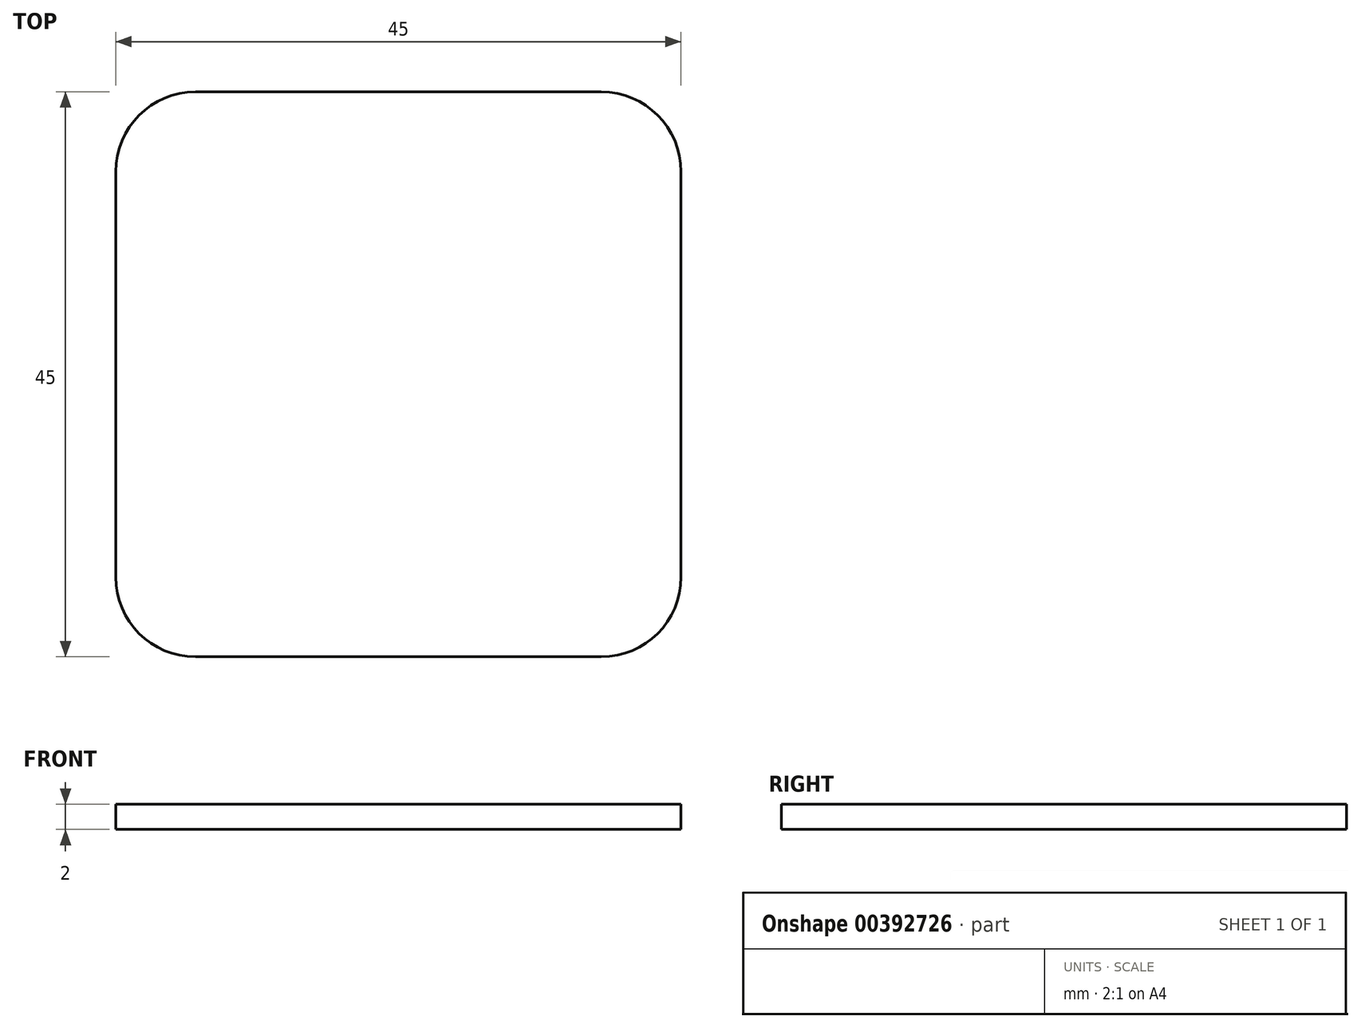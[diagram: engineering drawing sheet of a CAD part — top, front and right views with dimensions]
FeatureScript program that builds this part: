
annotation { "Feature Type Name" : "Feature", "Feature Type Description" : "" }
export const myFeature = defineFeature(function(context is Context, id is Id, definition is map)
    precondition{}
    {
        {
            var Q0;
            Q0=qCreatedBy(makeId("Top.planeOp"),FACE);
            var sketch = newSketch(context, id + "F0", { "sketchPlane" : qUnion([Q0])});
            skLineSegment(sketch, "E0.bottom", {"start": v(-9.36, -20.56) * mm, "end": v(-41.66, -20.56) * mm});
            skLineSegment(sketch, "E0.top", {"start": v(-9.36, 24.44) * mm, "end": v(-41.66, 24.44) * mm});
            skLineSegment(sketch, "E0.left", {"start": v(-3, -14.21) * mm, "end": v(-3, 18.09) * mm});
            skLineSegment(sketch, "E0.right", {"start": v(-48, -14.21) * mm, "end": v(-48, 18.09) * mm});
            skPoint(sketch, "E1.visualSharp", {"position": v(-48, 24.44) * mm});
            skArc(sketch, "E1.filletArc", {"start": v(-41.66, 24.44) * mm, "mid": v(-46.15, 22.58) * mm, "end": v(-48, 18.09) * mm});
            skPoint(sketch, "E2.visualSharp", {"position": v(-3, 24.44) * mm});
            skArc(sketch, "E2.filletArc", {"start": v(-3, 18.09) * mm, "mid": v(-4.87, 22.58) * mm, "end": v(-9.36, 24.44) * mm});
            skPoint(sketch, "E3.visualSharp", {"position": v(-3, -20.56) * mm});
            skArc(sketch, "E3.filletArc", {"start": v(-9.36, -20.56) * mm, "mid": v(-4.87, -18.7) * mm, "end": v(-3, -14.21) * mm});
            skPoint(sketch, "E4.visualSharp", {"position": v(-48, -20.56) * mm});
            skArc(sketch, "E4.filletArc", {"start": v(-48, -14.21) * mm, "mid": v(-46.15, -18.7) * mm, "end": v(-41.66, -20.56) * mm});
            skSolve(sketch);
        }
        {
            var Q0;
            Q0 = qSketchRegion(id + "F0", true);
            extrude(context, id + "F1", {"entities" : qUnion([Q0]), "depth" : 2 * mm});
        }
    });
